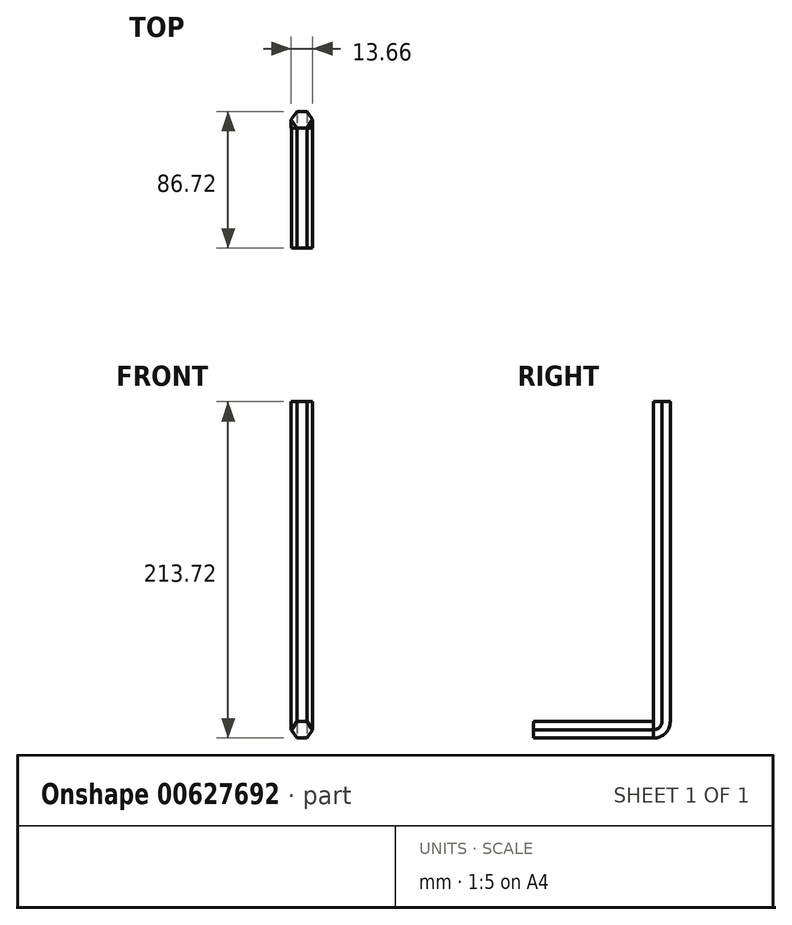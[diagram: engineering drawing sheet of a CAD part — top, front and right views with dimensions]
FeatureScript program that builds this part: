
annotation { "Feature Type Name" : "Feature", "Feature Type Description" : "" }
export const myFeature = defineFeature(function(context is Context, id is Id, definition is map)
    precondition{}
    {
        {
            var Q0;
            Q0=qCreatedBy(makeId("Front.planeOp"),FACE);
            var sketch = newSketch(context, id + "F0", { "sketchPlane" : qUnion([Q0])});
            skLineSegment(sketch, "E0.bottom", {"start": v(-3.17, -5.22) * mm, "end": v(3.18, -5.22) * mm});
            skLineSegment(sketch, "E0.top", {"start": v(-3.17, 5.22) * mm, "end": v(3.18, 5.22) * mm});
            skPoint(sketch, "E0.middle", {"position": v(0, 0) * mm});
            skLineSegment(sketch, "E1", {"start": v(-3.17, 5.22) * mm, "end": v(-6.57, 0) * mm});
            skLineSegment(sketch, "E2", {"start": v(-6.57, 0) * mm, "end": v(-3.17, -5.22) * mm});
            skLineSegment(sketch, "E3", {"start": v(3.17, 5.22) * mm, "end": v(6.79, 0) * mm});
            skLineSegment(sketch, "E4", {"start": v(3.17, -5.22) * mm, "end": v(6.79, 0) * mm});
            skSolve(sketch);
        }
        {
            var Q0;
            Q0 = qSketchRegion(id + "F0", true);
            extrude(context, id + "F1", {"entities" : qUnion([Q0]), "depth" : 76.2 * mm, "offsetDistance" : 25.4 * mm});
        }
        {
            var Q0;
            Q0=qCreatedBy(makeId("Front.planeOp"),FACE);
            var sketch = newSketch(context, id + "F2", { "sketchPlane" : qUnion([Q0])});
            skLineSegment(sketch, "E5.bottom", {"start": v(3.17, -5.26) * mm, "end": v(-3.17, -5.26) * mm});
            skLineSegment(sketch, "E5.top", {"start": v(3.17, 5.26) * mm, "end": v(-3.17, 5.26) * mm});
            skPoint(sketch, "E5.middle", {"position": v(0, 0) * mm});
            skLineSegment(sketch, "E6", {"start": v(-6.78, 0) * mm, "end": v(-3.18, -5.26) * mm});
            skLineSegment(sketch, "E7", {"start": v(3.17, -5.26) * mm, "end": v(6.88, 0) * mm});
            skLineSegment(sketch, "E8", {"start": v(3.17, 5.26) * mm, "end": v(6.88, 0) * mm});
            skLineSegment(sketch, "E9", {"start": v(-3.18, 5.26) * mm, "end": v(-6.78, 0) * mm});
            skSolve(sketch);
        }
        {
            var Q0;
            Q0=makeQuery(id+"F2.imprint","IMPRINT",FACE,{"disambiguationData":[TD([[makeQuery(id+"F2.imprint","IMPRINT",EDGE,{"derivedFrom":sQuery(id+"F2.wireOp",EDGE,"E5.bottom")}),-1.0]])]});
            var Q1;
            Q1=sQuery(id+"F2.wireOp",EDGE,"E5.top");
            revolve(context, id + "F3", {"operationType" : NewBodyOperationType.ADD, "entities" : qUnion([Q0]), "axis" : qUnion([Q1]), "revolveType" : RevolveType.ONE_DIRECTION, "oppositeDirection" : true, "angle" : 90 * degree});
        }
        {
            var Q0;
            Q0=makeQuery(id+"F3.opRevolve","CAP_FACE",FACE,{"disambiguationData":[OSD([sQuery(id+"F2.wireOp",EDGE,"E5.bottom"),sQuery(id+"F2.wireOp",EDGE,"E5.top"),sQuery(id+"F2.wireOp",EDGE,"E6"),sQuery(id+"F2.wireOp",EDGE,"E7"),sQuery(id+"F2.wireOp",EDGE,"E8"),sQuery(id+"F2.wireOp",EDGE,"E9")])],"isStart":false});
            extrude(context, id + "F4", {"entities" : qUnion([Q0]), "operationType" : NewBodyOperationType.ADD, "depth" : 203.2 * mm, "offsetDistance" : 25.4 * mm});
        }
    });
